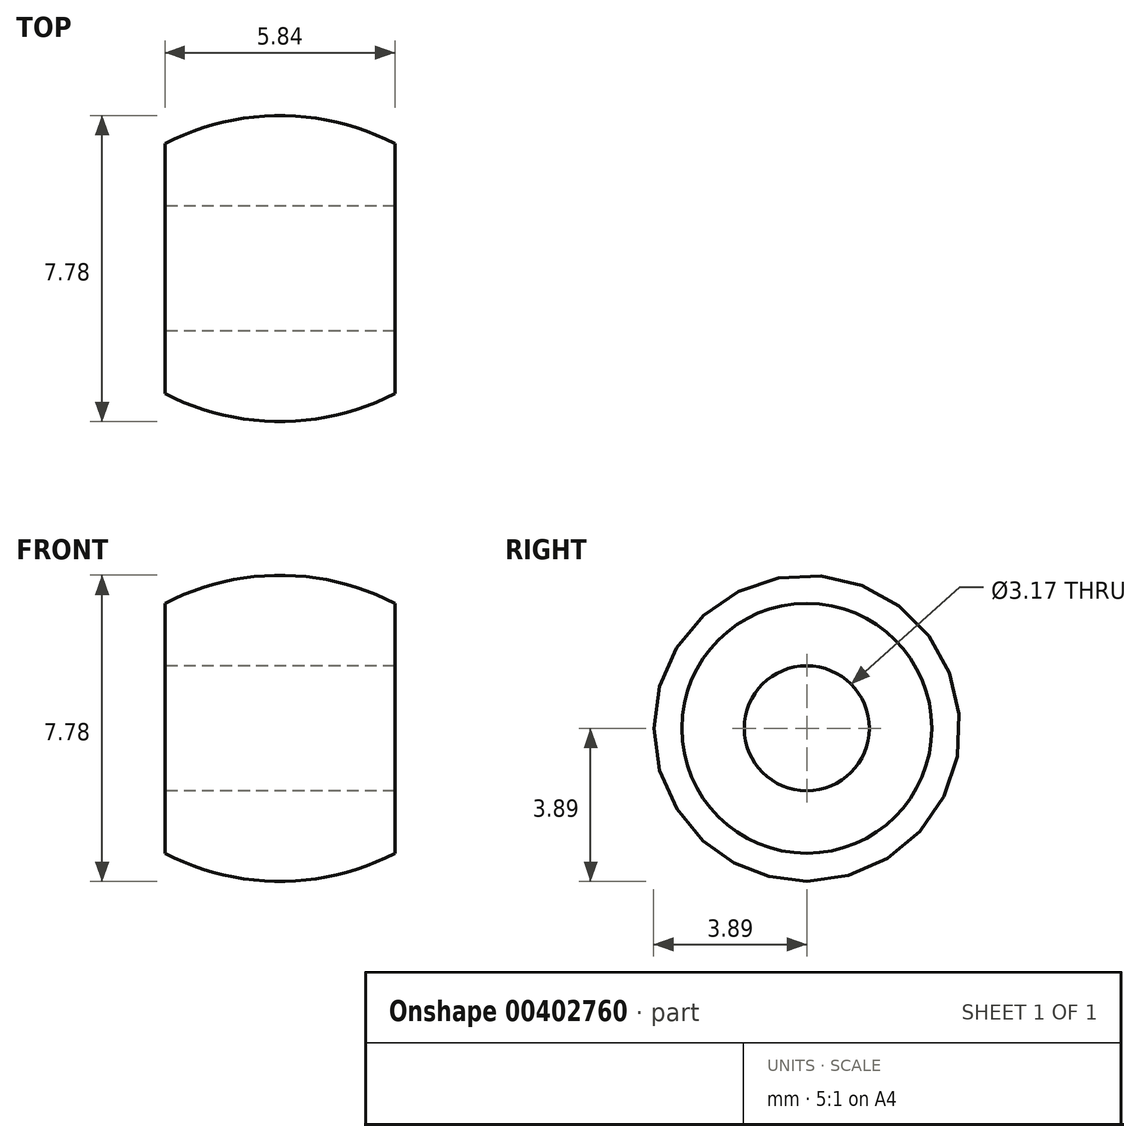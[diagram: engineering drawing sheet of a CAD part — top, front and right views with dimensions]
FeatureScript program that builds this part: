
annotation { "Feature Type Name" : "Feature", "Feature Type Description" : "" }
export const myFeature = defineFeature(function(context is Context, id is Id, definition is map)
    precondition{}
    {
        {
            var Q0;
            Q0=qCreatedBy(makeId("Right.planeOp"),FACE);
            var sketch = newSketch(context, id + "F0", { "sketchPlane" : qUnion([Q0])});
            skCircle(sketch, "E0", {"center": v(0, 0) * mm, "radius": 3.18 * mm});
            skCircle(sketch, "E1", {"center": v(0, 0) * mm, "radius": 1.59 * mm});
            skSolve(sketch);
        }
        {
            var Q0;
            Q0=makeQuery(id+"F0.imprint","IMPRINT",FACE,{"disambiguationData":[TD([[makeQuery(id+"F0.imprint","IMPRINT",EDGE,{"derivedFrom":sQuery(id+"F0.wireOp",EDGE,"E0")}),1.0]])]});
            extrude(context, id + "F1", {"entities" : qUnion([Q0]), "endBound" : BoundingType.SYMMETRIC, "depth" : 5.84 * mm, "offsetDistance" : 25.4 * mm});
        }
        {
            var Q0;
            Q0=qCreatedBy(makeId("Front.planeOp"),FACE);
            var sketch = newSketch(context, id + "F2", { "sketchPlane" : qUnion([Q0])});
            skArc(sketch, "E2", {"start": v(-2.92, 3.18) * mm, "mid": v(0, 3.89) * mm, "end": v(2.92, 3.18) * mm});
            skLineSegment(sketch, "E3", {"start": v(-2.92, 3.18) * mm, "end": v(2.92, 3.18) * mm});
            skLineSegment(sketch, "E4", {"start": v(0, 0) * mm, "end": v(-12.83, 0) * mm, "construction": true});
            skSolve(sketch);
        }
        {
            var Q0;
            Q0 = qSketchRegion(id + "F2", true);
            var Q1;
            Q1=sQuery(id+"F2.wireOp",EDGE,"E4");
            revolve(context, id + "F3", {"operationType" : NewBodyOperationType.ADD, "entities" : qUnion([Q0]), "axis" : qUnion([Q1]), "revolveType" : RevolveType.FULL});
        }
    });
